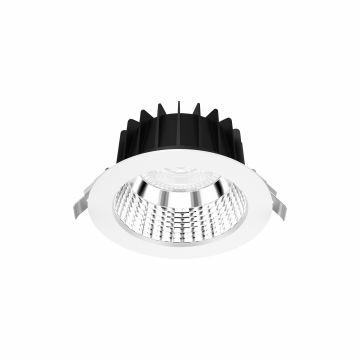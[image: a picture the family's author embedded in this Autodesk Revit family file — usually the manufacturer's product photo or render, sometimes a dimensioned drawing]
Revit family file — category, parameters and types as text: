
# Revit family: Lighting-Terziario-GEWISS-ELIA-AL-LED_INCASSO_ACCENTO_D172
name_source: partatom
category: Apparecchi per illuminazione
units: mm (PartAtom-declared; Revit-internal decimal feet)

## family parameters
Condiviso = No
Host = Superficie
Punto di calcolo locali = Sì
Quota connettore circolare = Usa diametro
Sorgente d'illuminazione = Sì
Taglio con vuoti quando caricato = No
Tipo di parte = Normale

## types (16) — shared parameters
Angolo inclinazione = -90.00°
Applicazione = Interno
Catalogo = LIGHTING
Catalogo Serie = ELIA AL
Classe isolamento = II
Colore = Bianco
Dimensioni (mm) = Standard
Emetti da lunghezza linea = 610 mm
FORO_CONTROSOFFITTO = 80 mm  [stored 0.262467 ft]
File diagramma fotometrico = GWF1411MH940.IES
Filtro dei colori = 16777215
Garanzia = 5 anni
Grado di protezione = IP40 - IP54
IDF = 5134b825-46db-4598-81aa-38e7782718ee
IDT = c1be2df2-232f-40c1-8cd1-aa0a19295d6b
Immagine tipo = ELIA_AL.jpg
Installazione = Incasso modulare
LARGHEZZA_FORO = 820 mm
LED = <Per categoria>
LED Life time (L80B50) = L80 B50 (Tq25°) = 50.000h
LUNGHEZZA FORO = 969 mm
L_lampada = 1500 mm
Lampada: = LED
POSIZIONE = 80000
Peso (kg) = 0,7
Peso (kg): = 0,7
Potenza di sistema = 25W
Produttore = GEWISS S.p.A.
Prospetto di default = 1219 mm
Resistenza agli urti = IK06
SEO = Incasso modulare
STRUTTURA = <Per categoria>
Scheda Tecnica = https://www.gewiss.com
Temperatura di funzionamento = -20° +45°
Temperatura di utilizzo = -20° +45°
Tensione = 220-240 VÂ
Tipo lampada = LED
Tipologia = Incasso modulare
Tipologia sorgente luminosa = LED - Non sostituibile
UGR: = UGR<19
URL = https://www.gewiss.com
Variazione temperatura colore lampada con luminosità attenuata = <Nessuno>
Versione file RFA = 20.0

## per-type parameters (varying)
| type | Descrizione | Lumen output (lm) | Modello | Ottica | Temperatura di colore | Temperatura di colore: |
| GWF1411MG930 - ELIA AL M2 30K 36° ST.ALONE DALI CRI90 | ELIA AL M2 30K 36° ST.ALONE DALI CRI90 | 2250 | GWF1411MG930 | 36° | 3000K | 3000K |
| GWF1410MH830 - ELIA AL M2 30K 60° ST.ALONE ON/OFF CRI80 | ELIA AL M2 30K 60° ST.ALONE ON/OFF CRI80 | 2600 | GWF1410MH830 | 60° | 3000K | 3000K |
| GWF1410MH930 - ELIA AL M2 30K 60° ST.ALONE ON/OFF CRI90 | ELIA AL M2 30K 60° ST.ALONE ON/OFF CRI90 | 2340 | GWF1410MH930 | 60° | 3000K | 3000K |
| GWF1410MG940 - ELIA AL M2 40K 36° ST.ALONE ON/OFF CRI90 | ELIA AL M2 40K 36° ST.ALONE ON/OFF CRI90 | 2430 | GWF1410MG940 | 36° | 4000K | 4000K |
| GWF1411MH930 - ELIA AL M2 30K 60° ST.ALONE DALI CRI90 | ELIA AL M2 30K 60° ST.ALONE DALI CRI90 | 2340 | GWF1411MH930 | 60° | 3000K | 3000K |
| GWF1410MG840 - ELIA AL M2 40K 36° ST.ALONE ON/OFF CRI80 | ELIA AL M2 40K 36° ST.ALONE ON/OFF CRI80 | 2700 | GWF1410MG840 | 36° | 4000K | 4000K |
| GWF1410MH940 - ELIA AL M2 40K 60° ST.ALONE ON/OFF CRI90 | ELIA AL M2 40K 60° ST.ALONE ON/OFF CRI90 | 2550 | GWF1410MH940 | 60° | 4000K | 4000K |
| GWF1411MG940 - ELIA AL M2 40K 36° ST.ALONE DALI CRI90 | ELIA AL M2 40K 36° ST.ALONE DALI CRI90 | 2430 | GWF1411MG940 | 36° | 4000K | 4000K |
| GWF1411MH940 - ELIA AL M2 40K 60° ST.ALONE DALI CRI90 | ELIA AL M2 40K 60° ST.ALONE DALI CRI90 | 2550 | GWF1411MH940 | 60° | 4000K | 4000K |
| GWF1411MG840 - ELIA AL M2 40K 36° ST.ALONE DALI CRI80 | ELIA AL M2 40K 36° ST.ALONE DALI CRI80 | 2700 | GWF1411MG840 | 36° | 4000K | 4000K |
| GWF1410MG930 - ELIA AL M2 30K 36° ST.ALONE ON/OFF CRI90 | ELIA AL M2 30K 36° ST.ALONE ON/OFF CRI90 | 2250 | GWF1410MG930 | 36° | 3000K | 3000K |
| GWF1411MH830 - ELIA AL M2 30K 60° ST.ALONE DALI CRI80 | ELIA AL M2 30K 60° ST.ALONE DALI CRI80 | 2600 | GWF1411MH830 | 60° | 3000K | 3000K |
| GWF1410MH840 - ELIA AL M2 40K 60° ST.ALONE ON/OFF CRI80 | ELIA AL M2 40K 60° ST.ALONE ON/OFF CRI80 | 2840 | GWF1410MH840 | 60° | 4000K | 4000K |
| GWF1410MG830 - ELIA AL M2 30K 36° ST.ALONE ON/OFF CRI80 | ELIA AL M2 30K 36° ST.ALONE ON/OFF CRI80 | 2500 | GWF1410MG830 | 36° | 3000K | 3000K |
| GWF1411MH840 - ELIA AL M2 40K 60° ST.ALONE DALI CRI80 | ELIA AL M2 40K 60° ST.ALONE DALI CRI80 | 2840 | GWF1411MH840 | 60° | 4000K | 4000K |
| GWF1411MG830 - ELIA AL M2 30K 36° ST.ALONE DALI CRI80 | ELIA AL M2 30K 36° ST.ALONE DALI CRI80 | 2500 | GWF1411MG830 | 36° | 3000K | 3000K |

note: [stored X ft] marks values corroborated as IEEE doubles in the binary element streams (Revit-internal decimal feet)
